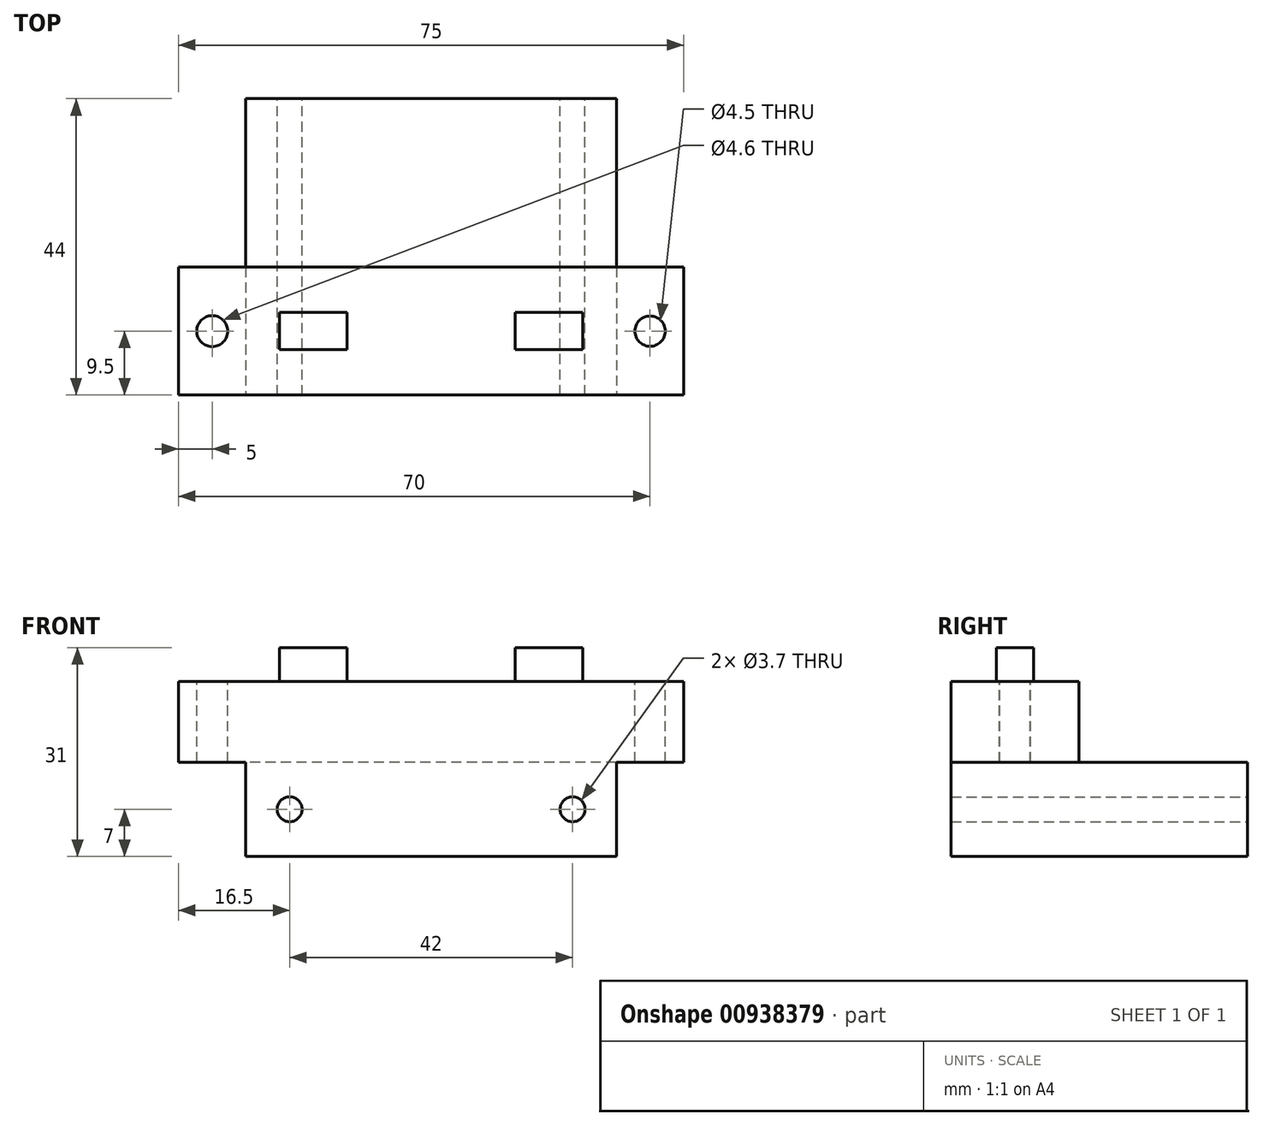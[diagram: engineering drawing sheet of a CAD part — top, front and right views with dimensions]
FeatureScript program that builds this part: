
annotation { "Feature Type Name" : "Feature", "Feature Type Description" : "" }
export const myFeature = defineFeature(function(context is Context, id is Id, definition is map)
    precondition{}
    {
        {
            var Q0;
            Q0=qCreatedBy(makeId("Top.planeOp"),FACE);
            var sketch = newSketch(context, id + "F0", { "sketchPlane" : qUnion([Q0])});
            skLineSegment(sketch, "E0.bottom", {"start": v(-27.5, 9.5) * mm, "end": v(27.5, 9.5) * mm});
            skLineSegment(sketch, "E0.top", {"start": v(-27.5, -9.5) * mm, "end": v(27.5, -9.5) * mm});
            skLineSegment(sketch, "E0.left", {"start": v(-27.5, 9.5) * mm, "end": v(-27.5, -9.5) * mm});
            skLineSegment(sketch, "E0.right", {"start": v(27.5, 9.5) * mm, "end": v(27.5, -9.5) * mm});
            skPoint(sketch, "E0.middle", {"position": v(0, 0) * mm});
            skSolve(sketch);
        }
        {
            var Q0;
            Q0=makeQuery(id+"F0.imprint","IMPRINT",FACE,{"disambiguationData":[TD([[makeQuery(id+"F0.imprint","IMPRINT",EDGE,{"derivedFrom":sQuery(id+"F0.wireOp",EDGE,"E0.bottom")}),-1.0]])]});
            extrude(context, id + "F1", {"entities" : qUnion([Q0]), "depth" : 26 * mm});
        }
        {
            var Q0;
            Q0=makeQuery(id+"F1.opExtrude","SWEPT_FACE",FACE,{"disambiguationData":[OSD([sQuery(id+"F0.wireOp",EDGE,"E0.bottom")])]});
            var sketch = newSketch(context, id + "F2", { "sketchPlane" : qUnion([Q0])});
            skLineSegment(sketch, "E1", {"start": v(-27.5, 14) * mm, "end": v(27.5, 14) * mm});
            skSolve(sketch);
        }
        {
            var Q0;
            {var subQ0=sQuery(id+"F2.wireOp",EDGE,"E1");Q0=makeQuery(id+"F2.imprint","IMPRINT",FACE,{"disambiguationData":[TD([[makeQuery(id+"F2.imprint","IMPRINT",EDGE,{"derivedFrom":subQ0}),-1.0]])]});}
            extrude(context, id + "F3", {"entities" : qUnion([Q0]), "operationType" : NewBodyOperationType.ADD, "depth" : 25 * mm});
        }
        {
            var Q0;
            {var subQ0=sQuery(id+"F0.wireOp",EDGE,"E0.left");Q0=makeQuery(id+"F3.boolean.opBoolean","MERGE",FACE,{"derivedFrom":[makeQuery(id+"F1.opExtrude","SWEPT_FACE",FACE,{"disambiguationData":[OSD([subQ0])]}),makeQuery(id+"F3.opExtrude","SWEPT_FACE",FACE,{"disambiguationData":[OSD([sQuery(id+"F0.wireOp",EDGE,"E0.bottom"),subQ0])]})]});}
            var sketch = newSketch(context, id + "F4", { "sketchPlane" : qUnion([Q0])});
            skLineSegment(sketch, "E2", {"start": v(-9.5, 14) * mm, "end": v(9.5, 14) * mm});
            skSolve(sketch);
        }
        {
            var Q0;
            Q0=qSketchRegion(id+"F4",true);
            var Q1;
            {var subQ0=sQuery(id+"F4.wireOp",EDGE,"E2");Q1=makeQuery(id+"F4.imprint","IMPRINT",FACE,{"disambiguationData":[TD([[makeQuery(id+"F4.imprint","IMPRINT",EDGE,{"derivedFrom":subQ0}),1.0]])]});}
            var Q2;
            {var subQ0=sQuery(id+"F0.wireOp",EDGE,"E0.right");Q2=makeQuery(id+"F3.boolean.opBoolean","MERGE",FACE,{"derivedFrom":[makeQuery(id+"F1.opExtrude","SWEPT_FACE",FACE,{"disambiguationData":[OSD([subQ0])]}),makeQuery(id+"F3.opExtrude","SWEPT_FACE",FACE,{"disambiguationData":[OSD([sQuery(id+"F0.wireOp",EDGE,"E0.bottom"),subQ0])]})]});}
            extrude(context, id + "F5", {"entities" : qUnion([Q0, Q1, Q2]), "operationType" : NewBodyOperationType.ADD, "depth" : 10 * mm});
        }
        {
            var Q0;
            {var subQ0=sQuery(id+"F0.wireOp",EDGE,"E0.right");Q0=makeQuery(id+"F3.boolean.opBoolean","MERGE",FACE,{"derivedFrom":[makeQuery(id+"F1.opExtrude","SWEPT_FACE",FACE,{"disambiguationData":[OSD([subQ0])]}),makeQuery(id+"F3.opExtrude","SWEPT_FACE",FACE,{"disambiguationData":[OSD([sQuery(id+"F0.wireOp",EDGE,"E0.bottom"),subQ0])]})]});}
            var sketch = newSketch(context, id + "F6", { "sketchPlane" : qUnion([Q0])});
            skLineSegment(sketch, "E3", {"start": v(9.5, 14) * mm, "end": v(-9.5, 14) * mm});
            skSolve(sketch);
        }
        {
            var Q0;
            {var subQ0=sQuery(id+"F6.wireOp",EDGE,"E3");Q0=makeQuery(id+"F6.imprint","IMPRINT",FACE,{"disambiguationData":[TD([[makeQuery(id+"F6.imprint","IMPRINT",EDGE,{"derivedFrom":subQ0}),-1.0]])]});}
            extrude(context, id + "F7", {"entities" : qUnion([Q0]), "operationType" : NewBodyOperationType.ADD, "depth" : 10 * mm});
        }
        {
            var Q0;
            Q0=makeQuery(id+"F3.opExtrude","CAP_FACE",FACE,{"disambiguationData":[OSD([sQuery(id+"F0.wireOp",EDGE,"E0.bottom"),sQuery(id+"F0.wireOp",EDGE,"E0.left"),sQuery(id+"F0.wireOp",EDGE,"E0.right"),sQuery(id+"F2.wireOp",EDGE,"E1")])],"isStart":false});
            var sketch = newSketch(context, id + "F8", { "sketchPlane" : qUnion([Q0])});
            skCircle(sketch, "E4", {"center": v(-21, 7) * mm, "radius": 1.85 * mm});
            skCircle(sketch, "E5", {"center": v(21, 7) * mm, "radius": 1.85 * mm});
            skSolve(sketch);
        }
        {
            var Q0;
            Q0=qSketchRegion(id+"F8",true);
            extrude(context, id + "F9", {"entities" : qUnion([Q0]), "operationType" : NewBodyOperationType.REMOVE, "oppositeDirection" : true, "depth" : 44 * mm});
        }
        {
            var Q0;
            Q0=qSketchRegion(id+"F8",true);
            extrude(context, id + "F10", {"entities" : qUnion([Q0]), "operationType" : NewBodyOperationType.REMOVE, "oppositeDirection" : true, "depth" : 44 * mm});
        }
        {
            var Q0;
            {var subQ0=sQuery(id+"F0.wireOp",EDGE,"E0.right");var subQ1=sQuery(id+"F0.wireOp",EDGE,"E0.left");Q0=makeQuery(id+"F7.boolean.opBoolean","MERGE",FACE,{"derivedFrom":[makeQuery(id+"F5.boolean.opBoolean","MERGE",FACE,{"derivedFrom":[makeQuery(id+"F1.opExtrude","CAP_FACE",FACE,{"disambiguationData":[OSD([sQuery(id+"F0.wireOp",EDGE,"E0.bottom"),sQuery(id+"F0.wireOp",EDGE,"E0.top"),subQ1,subQ0])],"isStart":false}),makeQuery(id+"F5.opExtrude","SWEPT_FACE",FACE,{"disambiguationData":[OSD([subQ1])]})]}),makeQuery(id+"F7.opExtrude","SWEPT_FACE",FACE,{"disambiguationData":[OSD([subQ0])]})]});}
            var sketch = newSketch(context, id + "F11", { "sketchPlane" : qUnion([Q0])});
            skCircle(sketch, "E6", {"center": v(-32.5, 0) * mm, "radius": 2.3 * mm});
            skCircle(sketch, "E7", {"center": v(32.5, 0) * mm, "radius": 2.25 * mm});
            skSolve(sketch);
        }
        {
            var Q0;
            Q0=makeQuery(id+"F11.imprint","IMPRINT",FACE,{"disambiguationData":[TD([[makeQuery(id+"F11.imprint","IMPRINT",EDGE,{"derivedFrom":sQuery(id+"F11.wireOp",EDGE,"E7")}),1.0]])]});
            var Q1;
            Q1=makeQuery(id+"F11.imprint","IMPRINT",FACE,{"disambiguationData":[TD([[makeQuery(id+"F11.imprint","IMPRINT",EDGE,{"derivedFrom":sQuery(id+"F11.wireOp",EDGE,"E6")}),1.0]])]});
            extrude(context, id + "F12", {"entities" : qUnion([Q0, Q1]), "operationType" : NewBodyOperationType.REMOVE, "oppositeDirection" : true, "depth" : 12 * mm});
        }
        {
            var Q0;
            {var subQ0=sQuery(id+"F0.wireOp",EDGE,"E0.right");var subQ1=sQuery(id+"F0.wireOp",EDGE,"E0.left");Q0=makeQuery(id+"F7.boolean.opBoolean","MERGE",FACE,{"derivedFrom":[makeQuery(id+"F5.boolean.opBoolean","MERGE",FACE,{"derivedFrom":[makeQuery(id+"F1.opExtrude","CAP_FACE",FACE,{"disambiguationData":[OSD([sQuery(id+"F0.wireOp",EDGE,"E0.bottom"),sQuery(id+"F0.wireOp",EDGE,"E0.top"),subQ1,subQ0])],"isStart":false}),makeQuery(id+"F5.opExtrude","SWEPT_FACE",FACE,{"disambiguationData":[OSD([subQ1])]})]}),makeQuery(id+"F7.opExtrude","SWEPT_FACE",FACE,{"disambiguationData":[OSD([subQ0])]})]});}
            var sketch = newSketch(context, id + "F13", { "sketchPlane" : qUnion([Q0])});
            skLineSegment(sketch, "E8.bottom", {"start": v(-22.5, 2.75) * mm, "end": v(-12.5, 2.75) * mm});
            skLineSegment(sketch, "E8.top", {"start": v(-22.5, -2.75) * mm, "end": v(-12.5, -2.75) * mm});
            skLineSegment(sketch, "E8.left", {"start": v(-22.5, 2.75) * mm, "end": v(-22.5, -2.75) * mm});
            skLineSegment(sketch, "E8.right", {"start": v(-12.5, 2.75) * mm, "end": v(-12.5, -2.75) * mm});
            skLineSegment(sketch, "E9.MirrorCS", {"start": v(12.5, 2.75) * mm, "end": v(12.5, -2.75) * mm});
            skLineSegment(sketch, "E10.MirrorCS", {"start": v(22.5, 2.75) * mm, "end": v(12.5, 2.75) * mm});
            skLineSegment(sketch, "E11.MirrorCS", {"start": v(22.5, 2.75) * mm, "end": v(22.5, -2.75) * mm});
            skLineSegment(sketch, "E12.MirrorCS", {"start": v(22.5, -2.75) * mm, "end": v(12.5, -2.75) * mm});
            skSolve(sketch);
        }
        {
            var Q0;
            Q0=makeQuery(id+"F13.imprint","IMPRINT",FACE,{"disambiguationData":[TD([[makeQuery(id+"F13.imprint","IMPRINT",EDGE,{"derivedFrom":sQuery(id+"F13.wireOp",EDGE,"E9.MirrorCS")}),1.0]])]});
            var Q1;
            Q1=makeQuery(id+"F13.imprint","IMPRINT",FACE,{"disambiguationData":[TD([[makeQuery(id+"F13.imprint","IMPRINT",EDGE,{"derivedFrom":sQuery(id+"F13.wireOp",EDGE,"E8.bottom")}),-1.0]])]});
            extrude(context, id + "F14", {"entities" : qUnion([Q0, Q1]), "operationType" : NewBodyOperationType.ADD, "depth" : 5 * mm});
        }
    });
